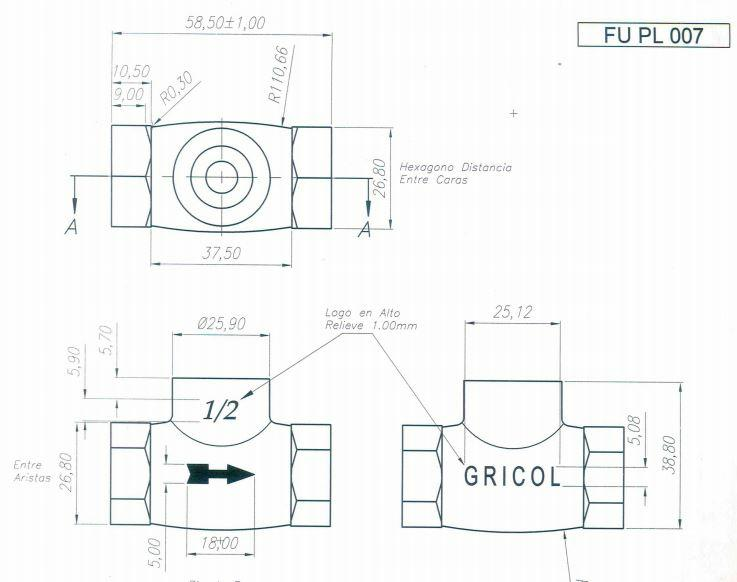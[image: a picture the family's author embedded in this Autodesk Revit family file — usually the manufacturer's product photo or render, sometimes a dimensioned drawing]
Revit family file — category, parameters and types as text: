
# Revit family: 01-1834-11 CONJUNTO REGISTRO DUCHA TEDESCA
name_source: partatom
category: Plumbing Fixtures
revit_build: Autodesk Revit 2018 (Build: 20170223_1515(x64)
units: mm (PartAtom-declared; Revit-internal decimal feet)

## family parameters
Cut with Voids When Loaded = No
Host = Face
OmniClass Number = 23.31.11.00
Part Type = Normal
Room Calculation Point = No
Round Connector Dimension = Use Diameter
Shared = No

## types (1)
- 01-1834-11
    Ancho escudo = 60 mm  [stored 0.19685 ft]
    CW Connection = Yes
    Default Elevation = 0 mm  [stored 0 ft]
    Description = Mezclador ducha
    HW Connection = Yes
    Laton = Laton
    Link Ficha Tecnica = No encontrada en internet
    Manija = 80 mm  [stored 0.262467 ft]
    Manufacturer = Gricol
    Model = 01-1834-11
    Plastico - ABS Cromado = Plastico - ABS Cromado
    Product Name = CONJUNTO REGISTRO DUCHA TEDESCA
    Type Image = LOGO-01.jpg
    URL = https://www.gricol.com
    Vent Connection = No
    Waste Connection = No

note: [stored X ft] marks values corroborated as IEEE doubles in the binary element streams (Revit-internal decimal feet)

## geometry (parser evidence)
native form markers: Blend x4, Sweep x24
no freeform markers — native parametric forms only
